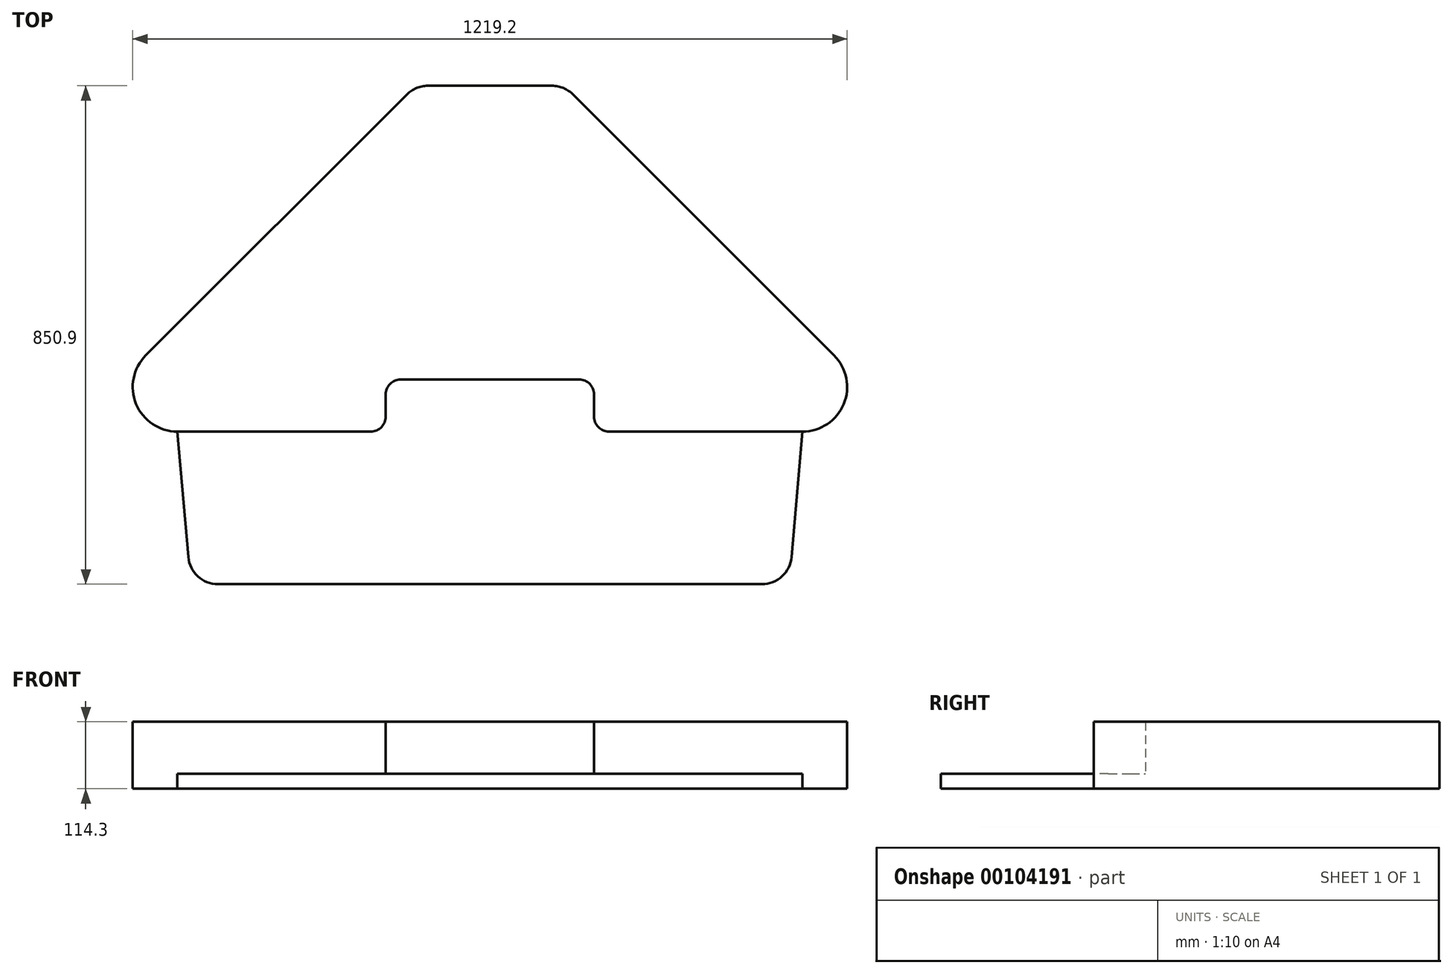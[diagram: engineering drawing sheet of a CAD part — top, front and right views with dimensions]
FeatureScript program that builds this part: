
annotation { "Feature Type Name" : "Feature", "Feature Type Description" : "" }
export const myFeature = defineFeature(function(context is Context, id is Id, definition is map)
    precondition{}
    {
        {
            var Q0;
            Q0=qCreatedBy(makeId("Top.planeOp"),FACE);
            var sketch = newSketch(context, id + "F0", { "sketchPlane" : qUnion([Q0])});
            skLineSegment(sketch, "E0", {"start": v(-127, 0) * mm, "end": v(127, 0) * mm});
            skLineSegment(sketch, "E1", {"start": v(127, 0) * mm, "end": v(587.28, -460.28) * mm});
            skLineSegment(sketch, "E2", {"start": v(-127, 0) * mm, "end": v(-587.28, -460.28) * mm});
            skArc(sketch, "E3", {"start": v(-587.28, -460.28) * mm, "mid": v(-603.8, -543.32) * mm, "end": v(-533.4, -590.36) * mm});
            skArc(sketch, "E4", {"start": v(587.28, -460.28) * mm, "mid": v(603.8, -543.32) * mm, "end": v(533.4, -590.36) * mm});
            skLineSegment(sketch, "E5", {"start": v(-533.4, -590.36) * mm, "end": v(-177.8, -590.36) * mm});
            skLineSegment(sketch, "E6", {"start": v(-177.8, -590.36) * mm, "end": v(-177.8, -501.65) * mm});
            skLineSegment(sketch, "E7", {"start": v(-177.8, -501.65) * mm, "end": v(177.8, -501.65) * mm});
            skLineSegment(sketch, "E8", {"start": v(177.8, -501.65) * mm, "end": v(177.8, -590.36) * mm});
            skLineSegment(sketch, "E9", {"start": v(177.8, -590.36) * mm, "end": v(533.4, -590.36) * mm});
            skLineSegment(sketch, "E10", {"start": v(0, 0) * mm, "end": v(0, -501.65) * mm, "construction": true});
            skLineSegment(sketch, "E11", {"start": v(-609.6, -78.4) * mm, "end": v(-609.6, -514.16) * mm, "construction": true});
            skLineSegment(sketch, "E12", {"start": v(-533.4, -590.36) * mm, "end": v(-510.6, -850.9) * mm});
            skLineSegment(sketch, "E13", {"start": v(-510.6, -850.9) * mm, "end": v(510.6, -850.9) * mm});
            skLineSegment(sketch, "E14", {"start": v(510.6, -850.9) * mm, "end": v(533.4, -590.36) * mm});
            skSolve(sketch);
        }
        {
            var Q0;
            Q0=makeQuery(id+"F0.imprint","IMPRINT",FACE,{"disambiguationData":[TD([[makeQuery(id+"F0.imprint","IMPRINT",EDGE,{"derivedFrom":sQuery(id+"F0.wireOp",EDGE,"E0")}),-1.0]])]});
            extrude(context, id + "F1", {"entities" : qUnion([Q0]), "depth" : 114.3 * mm});
        }
        {
            var Q0;
            Q0=makeQuery(id+"F0.imprint","IMPRINT",FACE,{"disambiguationData":[TD([[makeQuery(id+"F0.imprint","IMPRINT",EDGE,{"derivedFrom":sQuery(id+"F0.wireOp",EDGE,"E5")}),-1.0]])]});
            extrude(context, id + "F2", {"entities" : qUnion([Q0]), "operationType" : NewBodyOperationType.ADD, "depth" : 25.4 * mm});
        }
        {
            var Q0;
            Q0=makeQuery(id+"F1.opExtrude","SWEPT_EDGE",EDGE,{"disambiguationData":[OSD([sQuery(id+"F0.wireOp",EDGE,"E5"),sQuery(id+"F0.wireOp",EDGE,"E6")])]});
            var Q1;
            Q1=makeQuery(id+"F1.opExtrude","SWEPT_EDGE",EDGE,{"disambiguationData":[OSD([sQuery(id+"F0.wireOp",EDGE,"E8"),sQuery(id+"F0.wireOp",EDGE,"E9")])]});
            var Q2;
            Q2=makeQuery(id+"F1.opExtrude","SWEPT_EDGE",EDGE,{"disambiguationData":[OSD([sQuery(id+"F0.wireOp",EDGE,"E7"),sQuery(id+"F0.wireOp",EDGE,"E8")])]});
            var Q3;
            Q3=makeQuery(id+"F1.opExtrude","SWEPT_EDGE",EDGE,{"disambiguationData":[OSD([sQuery(id+"F0.wireOp",EDGE,"E6"),sQuery(id+"F0.wireOp",EDGE,"E7")])]});
            fillet(context, id + "F3", {"entities" : qUnion([Q0, Q1, Q2, Q3]), "radius" : 25.4 * mm, "tangentPropagation" : true, "allowEdgeOverflow" : false});
        }
        {
            var Q0;
            Q0=makeQuery(id+"F1.opExtrude","SWEPT_EDGE",EDGE,{"disambiguationData":[OSD([sQuery(id+"F0.wireOp",EDGE,"E0"),sQuery(id+"F0.wireOp",EDGE,"E2")])]});
            var Q1;
            Q1=makeQuery(id+"F1.opExtrude","SWEPT_EDGE",EDGE,{"disambiguationData":[OSD([sQuery(id+"F0.wireOp",EDGE,"E0"),sQuery(id+"F0.wireOp",EDGE,"E1")])]});
            var Q2;
            Q2=makeQuery(id+"F2.opExtrude","SWEPT_EDGE",EDGE,{"disambiguationData":[OSD([sQuery(id+"F0.wireOp",EDGE,"E12"),sQuery(id+"F0.wireOp",EDGE,"E13")])]});
            var Q3;
            Q3=makeQuery(id+"F2.opExtrude","SWEPT_EDGE",EDGE,{"disambiguationData":[OSD([sQuery(id+"F0.wireOp",EDGE,"E13"),sQuery(id+"F0.wireOp",EDGE,"E14")])]});
            fillet(context, id + "F4", {"entities" : qUnion([Q0, Q1, Q2, Q3]), "radius" : 50.8 * mm, "tangentPropagation" : true, "allowEdgeOverflow" : false});
        }
    });
